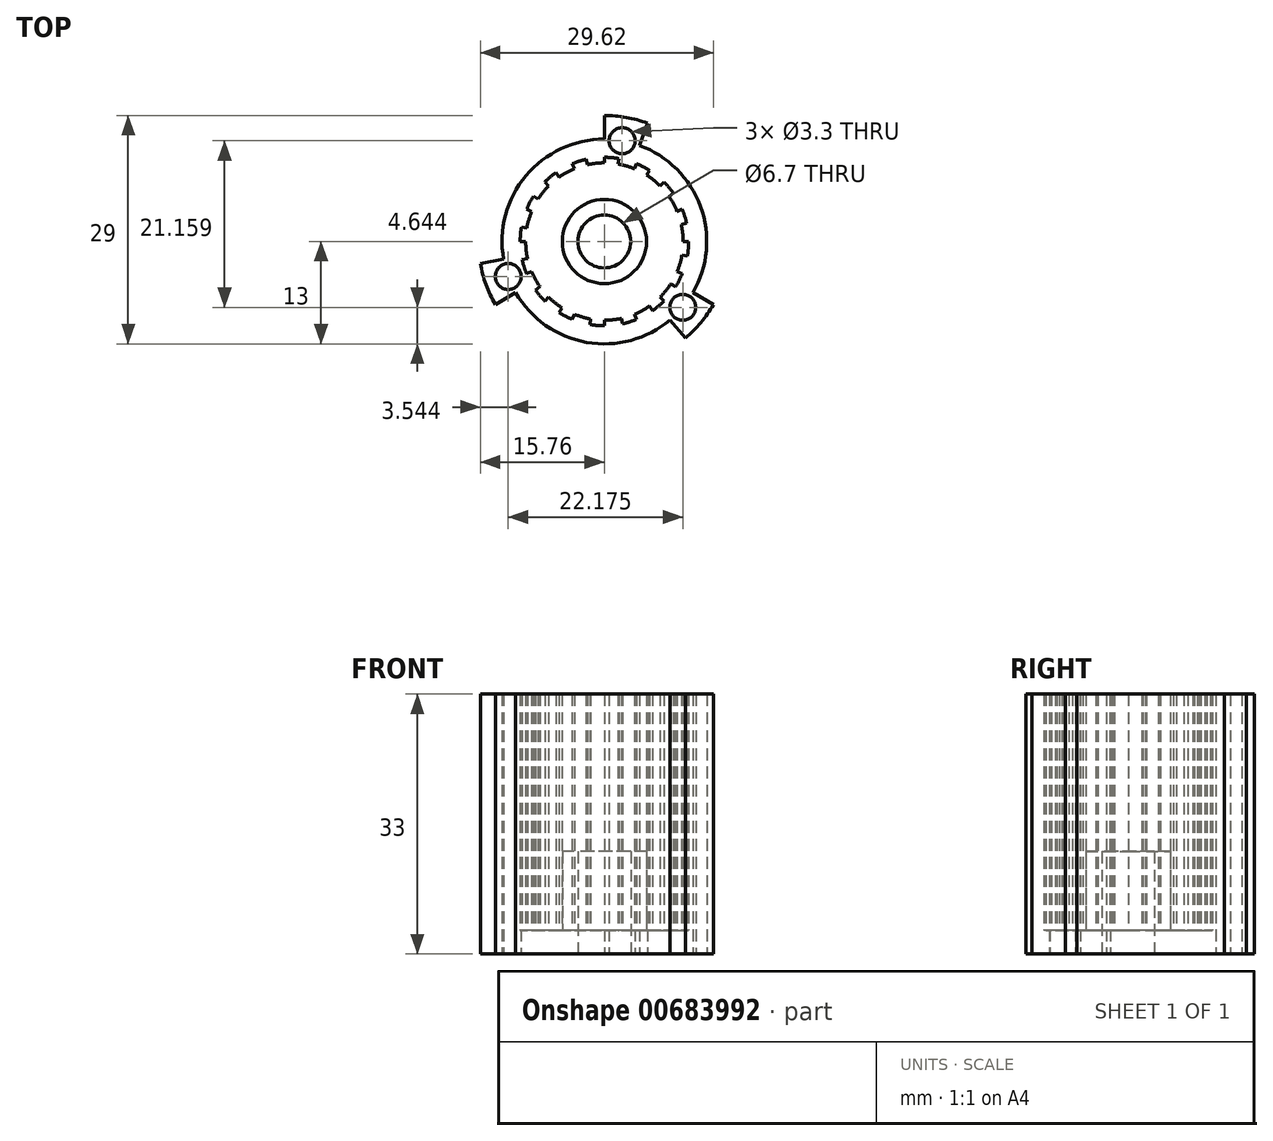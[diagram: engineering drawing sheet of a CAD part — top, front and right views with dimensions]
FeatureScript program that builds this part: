
annotation { "Feature Type Name" : "Feature", "Feature Type Description" : "" }
export const myFeature = defineFeature(function(context is Context, id is Id, definition is map)
    precondition{}
    {
        {
            var Q0;
            Q0=qCreatedBy(makeId("Top.planeOp"),FACE);
            var sketch = newSketch(context, id + "F0", { "sketchPlane" : qUnion([Q0])});
            skArc(sketch, "E0", {"start": v(-10, 0) * mm, "mid": v(9.96, -0.87) * mm, "end": v(-9.85, 1.74) * mm});
            skArc(sketch, "E1.0", {"start": v(-11.26, -6.5) * mm, "mid": v(-2.26, -12.8) * mm, "end": v(8.36, -9.96) * mm});
            skArc(sketch, "E2.0", {"start": v(5.47, 15.04) * mm, "mid": v(2.78, 15.76) * mm, "end": v(0, 16) * mm});
            skLineSegment(sketch, "E3", {"start": v(0, 13) * mm, "end": v(0, 16) * mm});
            skLineSegment(sketch, "E4", {"start": v(4.45, 12.22) * mm, "end": v(5.47, 15.04) * mm});
            skArc(sketch, "E5.1.0", {"start": v(-15.76, -2.78) * mm, "mid": v(-15.04, -5.47) * mm, "end": v(-13.86, -8) * mm});
            skLineSegment(sketch, "E5.1.1", {"start": v(-11.26, -6.5) * mm, "end": v(-13.86, -8) * mm});
            skLineSegment(sketch, "E5.1.2", {"start": v(-12.8, -2.26) * mm, "end": v(-15.76, -2.78) * mm});
            skArc(sketch, "E5.2.0", {"start": v(10.28, -12.26) * mm, "mid": v(12.26, -10.28) * mm, "end": v(13.86, -8) * mm});
            skLineSegment(sketch, "E5.2.1", {"start": v(11.26, -6.5) * mm, "end": v(13.86, -8) * mm});
            skLineSegment(sketch, "E5.2.2", {"start": v(8.36, -9.96) * mm, "end": v(10.28, -12.26) * mm});
            skCircle(sketch, "E6", {"center": v(2.26, 12.8) * mm, "radius": 1.65 * mm});
            skCircle(sketch, "E7", {"center": v(9.96, -8.36) * mm, "radius": 1.65 * mm});
            skCircle(sketch, "E8", {"center": v(-12.22, -4.45) * mm, "radius": 1.65 * mm});
            skArc(sketch, "E9.trimOffspring", {"start": v(11.26, -6.5) * mm, "mid": v(12.22, 4.45) * mm, "end": v(4.45, 12.22) * mm});
            skArc(sketch, "E10.trimOffspring", {"start": v(0, 13) * mm, "mid": v(-9.96, 8.36) * mm, "end": v(-12.8, -2.26) * mm});
            skCircle(sketch, "E11", {"center": v(0, 0) * mm, "radius": 5.35 * mm});
            skCircle(sketch, "E12.0", {"center": v(0, 0) * mm, "radius": 3.35 * mm});
            skArc(sketch, "E13.0", {"start": v(-10.54, 1.86) * mm, "mid": v(-10.66, 0.93) * mm, "end": v(-10.7, 0) * mm});
            skLineSegment(sketch, "E14.trimOffspring", {"start": v(-9.85, 1.74) * mm, "end": v(-10.54, 1.86) * mm});
            skLineSegment(sketch, "E15.trimOffspring", {"start": v(-10, 0) * mm, "end": v(-10.7, 0) * mm});
            skLineSegment(sketch, "E16.1.0", {"start": v(-9.24, 3.83) * mm, "end": v(-9.89, 4.1) * mm});
            skArc(sketch, "E16.1.1", {"start": v(-9.02, 5.75) * mm, "mid": v(-9.5, 4.94) * mm, "end": v(-9.89, 4.1) * mm});
            skLineSegment(sketch, "E16.1.2", {"start": v(-8.43, 5.37) * mm, "end": v(-9.02, 5.75) * mm});
            skLineSegment(sketch, "E16.2.0", {"start": v(-7.07, 7.07) * mm, "end": v(-7.57, 7.57) * mm});
            skArc(sketch, "E16.2.1", {"start": v(-6.14, 8.76) * mm, "mid": v(-6.88, 8.2) * mm, "end": v(-7.57, 7.57) * mm});
            skLineSegment(sketch, "E16.2.2", {"start": v(-5.74, 8.2) * mm, "end": v(-6.14, 8.76) * mm});
            skLineSegment(sketch, "E16.3.0", {"start": v(-3.83, 9.24) * mm, "end": v(-4.1, 9.89) * mm});
            skArc(sketch, "E16.3.1", {"start": v(-2.32, 10.45) * mm, "mid": v(-3.22, 10.2) * mm, "end": v(-4.1, 9.89) * mm});
            skLineSegment(sketch, "E16.3.2", {"start": v(-2.16, 9.76) * mm, "end": v(-2.32, 10.45) * mm});
            skLineSegment(sketch, "E16.4.0", {"start": v(0, 10) * mm, "end": v(0, 10.7) * mm});
            skArc(sketch, "E16.4.1", {"start": v(1.86, 10.54) * mm, "mid": v(0.93, 10.66) * mm, "end": v(0, 10.7) * mm});
            skLineSegment(sketch, "E16.4.2", {"start": v(1.74, 9.85) * mm, "end": v(1.86, 10.54) * mm});
            skLineSegment(sketch, "E16.5.0", {"start": v(3.83, 9.24) * mm, "end": v(4.1, 9.89) * mm});
            skArc(sketch, "E16.5.1", {"start": v(5.75, 9.02) * mm, "mid": v(4.94, 9.5) * mm, "end": v(4.1, 9.89) * mm});
            skLineSegment(sketch, "E16.5.2", {"start": v(5.37, 8.43) * mm, "end": v(5.75, 9.02) * mm});
            skLineSegment(sketch, "E16.6.0", {"start": v(7.07, 7.07) * mm, "end": v(7.57, 7.57) * mm});
            skArc(sketch, "E16.6.1", {"start": v(8.76, 6.14) * mm, "mid": v(8.2, 6.88) * mm, "end": v(7.57, 7.57) * mm});
            skLineSegment(sketch, "E16.6.2", {"start": v(8.2, 5.74) * mm, "end": v(8.76, 6.14) * mm});
            skLineSegment(sketch, "E16.7.0", {"start": v(9.24, 3.83) * mm, "end": v(9.89, 4.1) * mm});
            skArc(sketch, "E16.7.1", {"start": v(10.45, 2.32) * mm, "mid": v(10.2, 3.22) * mm, "end": v(9.89, 4.1) * mm});
            skLineSegment(sketch, "E16.7.2", {"start": v(9.76, 2.16) * mm, "end": v(10.45, 2.32) * mm});
            skLineSegment(sketch, "E16.8.0", {"start": v(10, 0) * mm, "end": v(10.7, 0) * mm});
            skArc(sketch, "E16.8.1", {"start": v(10.54, -1.86) * mm, "mid": v(10.66, -0.93) * mm, "end": v(10.7, 0) * mm});
            skLineSegment(sketch, "E16.8.2", {"start": v(9.85, -1.74) * mm, "end": v(10.54, -1.86) * mm});
            skLineSegment(sketch, "E16.9.0", {"start": v(9.24, -3.83) * mm, "end": v(9.89, -4.1) * mm});
            skArc(sketch, "E16.9.1", {"start": v(9.02, -5.75) * mm, "mid": v(9.5, -4.94) * mm, "end": v(9.89, -4.1) * mm});
            skLineSegment(sketch, "E16.9.2", {"start": v(8.43, -5.37) * mm, "end": v(9.02, -5.75) * mm});
            skLineSegment(sketch, "E16.10.0", {"start": v(7.07, -7.07) * mm, "end": v(7.57, -7.57) * mm});
            skArc(sketch, "E16.10.1", {"start": v(6.14, -8.76) * mm, "mid": v(6.88, -8.2) * mm, "end": v(7.57, -7.57) * mm});
            skLineSegment(sketch, "E16.10.2", {"start": v(5.74, -8.2) * mm, "end": v(6.14, -8.76) * mm});
            skLineSegment(sketch, "E16.11.0", {"start": v(3.83, -9.24) * mm, "end": v(4.1, -9.89) * mm});
            skArc(sketch, "E16.11.1", {"start": v(2.32, -10.45) * mm, "mid": v(3.22, -10.2) * mm, "end": v(4.1, -9.89) * mm});
            skLineSegment(sketch, "E16.11.2", {"start": v(2.16, -9.76) * mm, "end": v(2.32, -10.45) * mm});
            skLineSegment(sketch, "E16.12.0", {"start": v(0, -10) * mm, "end": v(0, -10.7) * mm});
            skArc(sketch, "E16.12.1", {"start": v(-1.86, -10.54) * mm, "mid": v(-0.93, -10.66) * mm, "end": v(0, -10.7) * mm});
            skLineSegment(sketch, "E16.12.2", {"start": v(-1.74, -9.85) * mm, "end": v(-1.86, -10.54) * mm});
            skLineSegment(sketch, "E16.13.0", {"start": v(-3.83, -9.24) * mm, "end": v(-4.1, -9.89) * mm});
            skArc(sketch, "E16.13.1", {"start": v(-5.75, -9.02) * mm, "mid": v(-4.94, -9.5) * mm, "end": v(-4.1, -9.89) * mm});
            skLineSegment(sketch, "E16.13.2", {"start": v(-5.37, -8.43) * mm, "end": v(-5.75, -9.02) * mm});
            skLineSegment(sketch, "E16.14.0", {"start": v(-7.07, -7.07) * mm, "end": v(-7.57, -7.57) * mm});
            skArc(sketch, "E16.14.1", {"start": v(-8.76, -6.14) * mm, "mid": v(-8.2, -6.88) * mm, "end": v(-7.57, -7.57) * mm});
            skLineSegment(sketch, "E16.14.2", {"start": v(-8.2, -5.74) * mm, "end": v(-8.76, -6.14) * mm});
            skLineSegment(sketch, "E16.15.0", {"start": v(-9.24, -3.83) * mm, "end": v(-9.89, -4.1) * mm});
            skArc(sketch, "E16.15.1", {"start": v(-10.45, -2.32) * mm, "mid": v(-10.2, -3.22) * mm, "end": v(-9.89, -4.1) * mm});
            skLineSegment(sketch, "E16.15.2", {"start": v(-9.76, -2.16) * mm, "end": v(-10.45, -2.32) * mm});
            skLineSegment(sketch, "E16.anchor1", {"start": v(0, 0) * mm, "end": v(-10.7, 0) * mm, "construction": true});
            skLineSegment(sketch, "E16.anchor2", {"start": v(0, 0) * mm, "end": v(-9.89, -4.1) * mm, "construction": true});
            skSolve(sketch);
        }
        {
            var Q0;
            Q0=makeQuery(id+"F0.imprint","IMPRINT",FACE,{"disambiguationData":[TD([[makeQuery(id+"F0.imprint","IMPRINT",EDGE,{"derivedFrom":sQuery(id+"F0.wireOp",EDGE,"E0")}),1.0]])]});
            var Q1;
            Q1=makeQuery(id+"F0.imprint","IMPRINT",FACE,{"disambiguationData":[TD([[makeQuery(id+"F0.imprint","IMPRINT",EDGE,{"derivedFrom":sQuery(id+"F0.wireOp",EDGE,"E0")}),-1.0]])]});
            extrude(context, id + "F1", {"entities" : qUnion([Q0, Q1]), "depth" : 3 * mm, "offsetDistance" : 25 * mm});
        }
        {
            var Q0;
            Q0=makeQuery(id+"F0.imprint","IMPRINT",FACE,{"disambiguationData":[TD([[makeQuery(id+"F0.imprint","IMPRINT",EDGE,{"derivedFrom":sQuery(id+"F0.wireOp",EDGE,"E0")}),-1.0]])]});
            extrude(context, id + "F2", {"entities" : qUnion([Q0]), "operationType" : NewBodyOperationType.ADD, "depth" : 33 * mm, "offsetDistance" : 25 * mm});
        }
        {
            var Q0;
            Q0=makeQuery(id+"F0.imprint","IMPRINT",FACE,{"disambiguationData":[TD([[makeQuery(id+"F0.imprint","IMPRINT",EDGE,{"derivedFrom":sQuery(id+"F0.wireOp",EDGE,"E11")}),1.0]])]});
            extrude(context, id + "F3", {"entities" : qUnion([Q0]), "operationType" : NewBodyOperationType.ADD, "depth" : 13 * mm, "offsetDistance" : 25 * mm});
        }
        {
            var Q0;
            {var subQ0=sQuery(id+"F0.wireOp",EDGE,"E16.4.0");Q0=makeQuery(id+"F0.imprint","IMPRINT",FACE,{"disambiguationData":[TD([[makeQuery(id+"F0.imprint","IMPRINT",EDGE,{"derivedFrom":subQ0}),-1.0]])]});}
            var Q1;
            {var subQ0=sQuery(id+"F0.wireOp",EDGE,"E16.3.0");Q1=makeQuery(id+"F0.imprint","IMPRINT",FACE,{"disambiguationData":[TD([[makeQuery(id+"F0.imprint","IMPRINT",EDGE,{"derivedFrom":subQ0}),-1.0]])]});}
            var Q2;
            {var subQ0=sQuery(id+"F0.wireOp",EDGE,"E16.2.0");Q2=makeQuery(id+"F0.imprint","IMPRINT",FACE,{"disambiguationData":[TD([[makeQuery(id+"F0.imprint","IMPRINT",EDGE,{"derivedFrom":subQ0}),-1.0]])]});}
            var Q3;
            {var subQ0=sQuery(id+"F0.wireOp",EDGE,"E16.1.0");Q3=makeQuery(id+"F0.imprint","IMPRINT",FACE,{"disambiguationData":[TD([[makeQuery(id+"F0.imprint","IMPRINT",EDGE,{"derivedFrom":subQ0}),-1.0]])]});}
            var Q4;
            {var subQ0=sQuery(id+"F0.wireOp",EDGE,"E16.5.0");Q4=makeQuery(id+"F0.imprint","IMPRINT",FACE,{"disambiguationData":[TD([[makeQuery(id+"F0.imprint","IMPRINT",EDGE,{"derivedFrom":subQ0}),-1.0]])]});}
            var Q5;
            {var subQ0=sQuery(id+"F0.wireOp",EDGE,"E16.6.0");Q5=makeQuery(id+"F0.imprint","IMPRINT",FACE,{"disambiguationData":[TD([[makeQuery(id+"F0.imprint","IMPRINT",EDGE,{"derivedFrom":subQ0}),-1.0]])]});}
            var Q6;
            {var subQ0=sQuery(id+"F0.wireOp",EDGE,"E16.7.0");Q6=makeQuery(id+"F0.imprint","IMPRINT",FACE,{"disambiguationData":[TD([[makeQuery(id+"F0.imprint","IMPRINT",EDGE,{"derivedFrom":subQ0}),-1.0]])]});}
            var Q7;
            {var subQ0=sQuery(id+"F0.wireOp",EDGE,"E16.8.0");Q7=makeQuery(id+"F0.imprint","IMPRINT",FACE,{"disambiguationData":[TD([[makeQuery(id+"F0.imprint","IMPRINT",EDGE,{"derivedFrom":subQ0}),-1.0]])]});}
            var Q8;
            {var subQ0=sQuery(id+"F0.wireOp",EDGE,"E16.9.0");Q8=makeQuery(id+"F0.imprint","IMPRINT",FACE,{"disambiguationData":[TD([[makeQuery(id+"F0.imprint","IMPRINT",EDGE,{"derivedFrom":subQ0}),-1.0]])]});}
            var Q9;
            {var subQ0=sQuery(id+"F0.wireOp",EDGE,"E16.10.0");Q9=makeQuery(id+"F0.imprint","IMPRINT",FACE,{"disambiguationData":[TD([[makeQuery(id+"F0.imprint","IMPRINT",EDGE,{"derivedFrom":subQ0}),-1.0]])]});}
            var Q10;
            {var subQ0=sQuery(id+"F0.wireOp",EDGE,"E16.11.0");Q10=makeQuery(id+"F0.imprint","IMPRINT",FACE,{"disambiguationData":[TD([[makeQuery(id+"F0.imprint","IMPRINT",EDGE,{"derivedFrom":subQ0}),-1.0]])]});}
            var Q11;
            {var subQ0=sQuery(id+"F0.wireOp",EDGE,"E16.12.0");Q11=makeQuery(id+"F0.imprint","IMPRINT",FACE,{"disambiguationData":[TD([[makeQuery(id+"F0.imprint","IMPRINT",EDGE,{"derivedFrom":subQ0}),-1.0]])]});}
            var Q12;
            {var subQ0=sQuery(id+"F0.wireOp",EDGE,"E16.13.0");Q12=makeQuery(id+"F0.imprint","IMPRINT",FACE,{"disambiguationData":[TD([[makeQuery(id+"F0.imprint","IMPRINT",EDGE,{"derivedFrom":subQ0}),-1.0]])]});}
            var Q13;
            {var subQ0=sQuery(id+"F0.wireOp",EDGE,"E16.14.0");Q13=makeQuery(id+"F0.imprint","IMPRINT",FACE,{"disambiguationData":[TD([[makeQuery(id+"F0.imprint","IMPRINT",EDGE,{"derivedFrom":subQ0}),-1.0]])]});}
            var Q14;
            {var subQ0=sQuery(id+"F0.wireOp",EDGE,"E16.15.0");Q14=makeQuery(id+"F0.imprint","IMPRINT",FACE,{"disambiguationData":[TD([[makeQuery(id+"F0.imprint","IMPRINT",EDGE,{"derivedFrom":subQ0}),-1.0]])]});}
            extrude(context, id + "F4", {"entities" : qUnion([Q0, Q1, Q2, Q3, Q4, Q5, Q6, Q7, Q8, Q9, Q10, Q11, Q12, Q13, Q14]), "operationType" : NewBodyOperationType.ADD, "depth" : 3 * mm, "offsetDistance" : 25 * mm});
        }
    });
